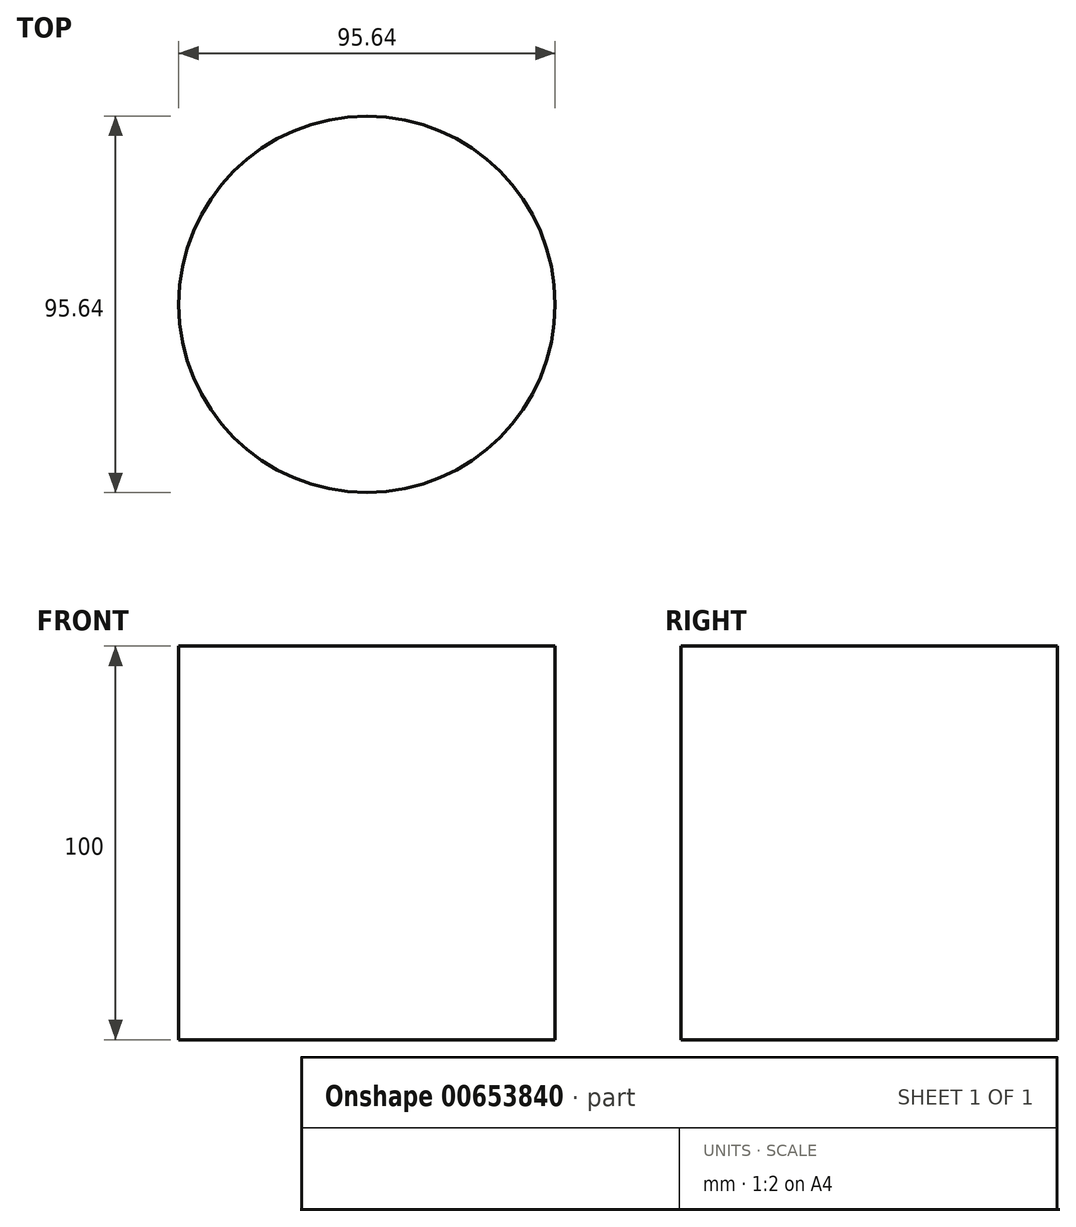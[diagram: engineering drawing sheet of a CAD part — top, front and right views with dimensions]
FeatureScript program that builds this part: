
annotation { "Feature Type Name" : "Feature", "Feature Type Description" : "" }
export const myFeature = defineFeature(function(context is Context, id is Id, definition is map)
    precondition{}
    {
        {
            var Q0;
            Q0=qCreatedBy(makeId("Top.planeOp"),FACE);
            var sketch = newSketch(context, id + "F0", { "sketchPlane" : qUnion([Q0])});
            skCircle(sketch, "E0", {"center": v(0, 0) * mm, "radius": 47.82 * mm});
            skSolve(sketch);
        }
        {
            var Q0;
            Q0=makeQuery(id+"F0.imprint","IMPRINT",FACE,{"disambiguationData":[TD([[makeQuery(id+"F0.imprint","IMPRINT",EDGE,{"derivedFrom":sQuery(id+"F0.wireOp",EDGE,"E0")}),1.0]])]});
            extrude(context, id + "F1", {"entities" : qUnion([Q0]), "depth" : 100 * mm, "offsetDistance" : 25.4 * mm});
        }
        {
            var Q0;
            Q0=makeQuery(id+"F1.opExtrude","CAP_FACE",FACE,{"disambiguationData":[OSD([sQuery(id+"F0.wireOp",EDGE,"E0")])],"isStart":false});
            var sketch = newSketch(context, id + "F2", { "sketchPlane" : qUnion([Q0])});
            skSolve(sketch);
        }
    });
